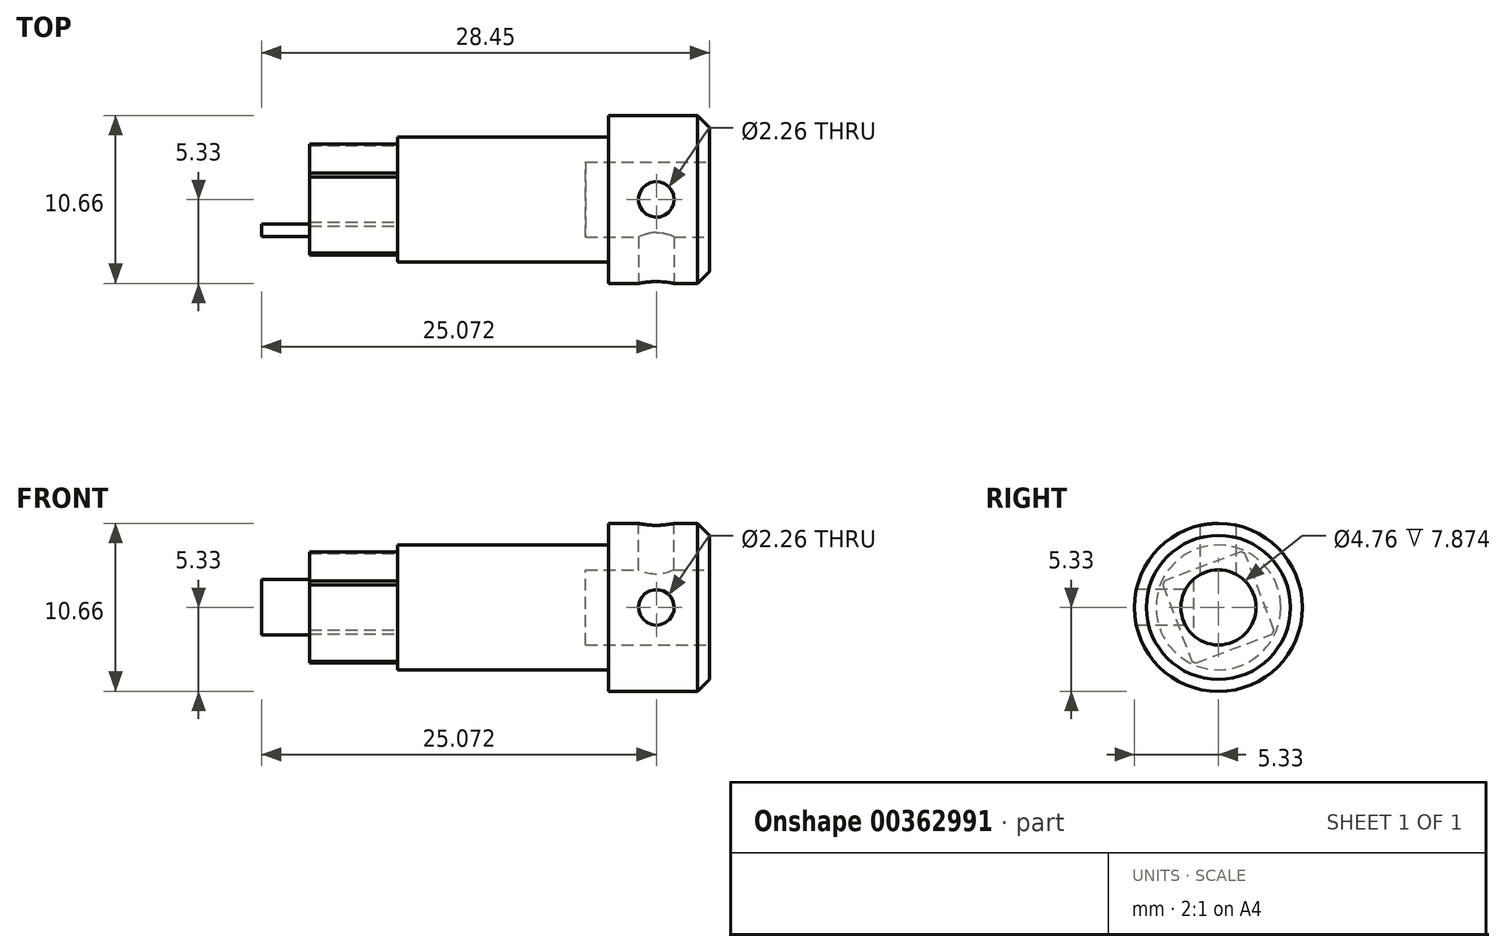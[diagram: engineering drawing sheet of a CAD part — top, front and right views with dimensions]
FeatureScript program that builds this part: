
annotation { "Feature Type Name" : "Feature", "Feature Type Description" : "" }
export const myFeature = defineFeature(function(context is Context, id is Id, definition is map)
    precondition{}
    {
        {
            var Q0;
            Q0=qCreatedBy(makeId("Right.planeOp"),FACE);
            var sketch = newSketch(context, id + "F0", { "sketchPlane" : qUnion([Q0])});
            skCircle(sketch, "E0", {"center": v(0, 0) * mm, "radius": 5.33 * mm});
            skSolve(sketch);
        }
        {
            var Q0;
            Q0=makeQuery(id+"F0.imprint","IMPRINT",FACE,{"disambiguationData":[TD([[makeQuery(id+"F0.imprint","IMPRINT",EDGE,{"derivedFrom":sQuery(id+"F0.wireOp",EDGE,"E0")}),1.0]])]});
            extrude(context, id + "F1", {"entities" : qUnion([Q0]), "oppositeDirection" : true, "depth" : 6.43 * mm});
        }
        {
            var Q0;
            Q0=makeQuery(id+"F1.opExtrude","CAP_FACE",FACE,{"disambiguationData":[OSD([sQuery(id+"F0.wireOp",EDGE,"E0")])],"isStart":false});
            var sketch = newSketch(context, id + "F2", { "sketchPlane" : qUnion([Q0])});
            skCircle(sketch, "E1", {"center": v(0, 0) * mm, "radius": 3.96 * mm});
            skSolve(sketch);
        }
        {
            var Q0;
            Q0=makeQuery(id+"F2.imprint","IMPRINT",FACE,{"disambiguationData":[TD([[makeQuery(id+"F2.imprint","IMPRINT",EDGE,{"derivedFrom":sQuery(id+"F2.wireOp",EDGE,"E1")}),1.0]])]});
            extrude(context, id + "F3", {"entities" : qUnion([Q0]), "operationType" : NewBodyOperationType.ADD, "depth" : 13.4 * mm});
        }
        {
            var Q0;
            Q0=makeQuery(id+"F3.opExtrude","CAP_FACE",FACE,{"disambiguationData":[OSD([sQuery(id+"F2.wireOp",EDGE,"E1")])],"isStart":false});
            var sketch = newSketch(context, id + "F4", { "sketchPlane" : qUnion([Q0])});
            skCircle(sketch, "E2.cCircle", {"center": v(0, 0) * mm, "radius": 2.8 * mm, "construction": true});
            skLineSegment(sketch, "E2.0", {"start": v(-1.62, 3.6) * mm, "end": v(3.6, 1.62) * mm});
            skLineSegment(sketch, "E2.1", {"start": v(3.6, 1.62) * mm, "end": v(1.62, -3.6) * mm});
            skLineSegment(sketch, "E2.2", {"start": v(1.62, -3.6) * mm, "end": v(-3.6, -1.62) * mm});
            skLineSegment(sketch, "E2.3", {"start": v(-3.6, -1.62) * mm, "end": v(-1.62, 3.6) * mm});
            skPoint(sketch, "E2.0.midPoint", {"position": v(1, 2.61) * mm});
            skCircle(sketch, "E3", {"center": v(0, 0) * mm, "radius": 3.81 * mm});
            skSolve(sketch);
        }
        {
            var Q0;
            {var subQ0=sQuery(id+"F4.wireOp",EDGE,"E3");var subQ10=sQuery(id+"F4.wireOp",EDGE,"E2.0");var subQ11=makeQuery(id+"F4.imprint","INTERSECT",VERTEX,{"disambiguationData":[OD(0.0)],"derivedFrom":[subQ10,subQ0]});Q0=makeQuery(id+"F4.imprint","IMPRINT",FACE,{"disambiguationData":[TD([[makeQuery(id+"F4.imprint","IMPRINT",EDGE,{"disambiguationData":[TD([[subQ11,-1.0]])],"derivedFrom":subQ10}),-1.0]])]});}
            extrude(context, id + "F5", {"entities" : qUnion([Q0]), "operationType" : NewBodyOperationType.ADD, "depth" : 5.6 * mm});
        }
        {
            var Q0;
            Q0=makeQuery(id+"F5.opExtrude","CAP_FACE",FACE,{"disambiguationData":[OSD([sQuery(id+"F4.wireOp",EDGE,"E2.0"),sQuery(id+"F4.wireOp",EDGE,"E2.1"),sQuery(id+"F4.wireOp",EDGE,"E2.2"),sQuery(id+"F4.wireOp",EDGE,"E2.3"),sQuery(id+"F4.wireOp",EDGE,"E3")])],"isStart":false});
            var sketch = newSketch(context, id + "F6", { "sketchPlane" : qUnion([Q0])});
            skCircle(sketch, "E4", {"center": v(0, 0) * mm, "radius": 2.36 * mm});
            skLineSegment(sketch, "E5.0", {"start": v(1.57, 6.6) * mm, "end": v(1.57, -8.04) * mm});
            skSolve(sketch);
        }
        {
            var Q0;
            {var subQ0=sQuery(id+"F6.wireOp",EDGE,"E5.0");var subQ1=sQuery(id+"F6.wireOp",EDGE,"E4");var subQ2=makeQuery(id+"F6.imprint","INTERSECT",VERTEX,{"disambiguationData":[OD(0.0)],"derivedFrom":[subQ1,subQ0]});Q0=makeQuery(id+"F6.imprint","IMPRINT",FACE,{"disambiguationData":[TD([[makeQuery(id+"F6.imprint","IMPRINT",EDGE,{"disambiguationData":[TD([[subQ2,-1.0]])],"derivedFrom":subQ1}),1.0]])]});}
            extrude(context, id + "F7", {"entities" : qUnion([Q0]), "operationType" : NewBodyOperationType.ADD, "depth" : 3.05 * mm});
        }
        {
            var Q0;
            Q0=makeQuery(id+"F1.opExtrude","CAP_EDGE",EDGE,{"disambiguationData":[OSD([sQuery(id+"F0.wireOp",EDGE,"E0")])],"isStart":true});
            chamfer(context, id + "F8", {"entities" : qUnion([Q0]), "chamferType" : ChamferType.OFFSET_ANGLE, "width" : 0.76 * mm, "oppositeDirection" : false, "angle" : 45 * degree, "tangentPropagation" : true});
        }
        {
            var Q0;
            Q0=makeQuery(id+"F1.opExtrude","CAP_FACE",FACE,{"disambiguationData":[OSD([sQuery(id+"F0.wireOp",EDGE,"E0")])],"isStart":true});
            var sketch = newSketch(context, id + "F9", { "sketchPlane" : qUnion([Q0])});
            skCircle(sketch, "E6", {"center": v(0, 0) * mm, "radius": 2.38 * mm});
            skSolve(sketch);
        }
        {
            var Q0;
            Q0=makeQuery(id+"F9.imprint","IMPRINT",FACE,{"disambiguationData":[TD([[makeQuery(id+"F9.imprint","IMPRINT",EDGE,{"derivedFrom":sQuery(id+"F9.wireOp",EDGE,"E6")}),1.0]])]});
            extrude(context, id + "F10", {"entities" : qUnion([Q0]), "operationType" : NewBodyOperationType.REMOVE, "oppositeDirection" : true, "depth" : 7.87 * mm});
        }
        {
            var Q0;
            Q0=qCreatedBy(makeId("Front.planeOp"),FACE);
            cPlane(context, id + "F11", {"entities" : qUnion([Q0]), "cplaneType" : CPlaneType.OFFSET, "offset" : 5.33 * mm, "width" : 152.4 * mm, "height" : 152.4 * mm});
        }
        {
            var Q0;
            Q0=qCreatedBy(id+"F11.planeOp",FACE);
            var sketch = newSketch(context, id + "F12", { "sketchPlane" : qUnion([Q0])});
            skPoint(sketch, "E7", {"position": v(-3.38, 0) * mm});
            skSolve(sketch);
        }
        {
            var Q0;
            Q0=sQuery(id+"F12.wireOp",VERTEX,"E7");
            var Q1;
            Q1=makeQuery(id+"F1.opExtrude","SWEPT_BODY",BODY,{"disambiguationData":[OSD([sQuery(id+"F0.wireOp",EDGE,"E0")])]});
            hole(context, id + "F13", {"style" : HoleStyle.SIMPLE, "endStyle" : HoleEndStyle.BLIND, "standardTappedOrClearance" : lookupTablePath({ "standard" : "ANSI", "engagement" : "75%", "pitch" : "40 tpi", "size" : "#4", "type" : "Tapped" }), "standardBlindInLast" : lookupTablePath({ "standard" : "ANSI", "engagement" : "75%", "pitch" : "40 tpi", "size" : "#4", "type" : "Tapped" }), "holeDiameter" : 2.26 * mm, "showTappedDepth" : true, "holeDepth" : 6.48 * mm, "tappedDepth" : 4.57 * mm, "tapClearance" : 3, "locations" : qUnion([Q0]), "scope" : qUnion([Q1]), "majorDiameter" : 2.84 * mm});
        }
        {
            var Q0;
            Q0=qCreatedBy(makeId("Top.planeOp"),FACE);
            cPlane(context, id + "F14", {"entities" : qUnion([Q0]), "cplaneType" : CPlaneType.OFFSET, "offset" : 5.33 * mm, "width" : 152.4 * mm, "height" : 152.4 * mm});
        }
        {
            var Q0;
            Q0=qCreatedBy(id+"F14.planeOp",FACE);
            var sketch = newSketch(context, id + "F15", { "sketchPlane" : qUnion([Q0])});
            skPoint(sketch, "E8", {"position": v(-3.38, 0) * mm});
            skSolve(sketch);
        }
        {
            var Q0;
            Q0=sQuery(id+"F15.wireOp",VERTEX,"E8");
            var Q1;
            Q1=makeQuery(id+"F1.opExtrude","SWEPT_BODY",BODY,{"disambiguationData":[OSD([sQuery(id+"F0.wireOp",EDGE,"E0")])]});
            hole(context, id + "F16", {"style" : HoleStyle.SIMPLE, "endStyle" : HoleEndStyle.BLIND, "standardTappedOrClearance" : lookupTablePath({ "standard" : "ANSI", "engagement" : "75%", "pitch" : "40 tpi", "size" : "#4", "type" : "Tapped" }), "standardBlindInLast" : lookupTablePath({ "standard" : "ANSI", "engagement" : "75%", "pitch" : "40 tpi", "size" : "#4", "type" : "Tapped" }), "holeDiameter" : 2.26 * mm, "showTappedDepth" : true, "holeDepth" : 6.48 * mm, "tappedDepth" : 4.57 * mm, "tapClearance" : 3, "locations" : qUnion([Q0]), "scope" : qUnion([Q1]), "majorDiameter" : 2.84 * mm});
        }
    });
